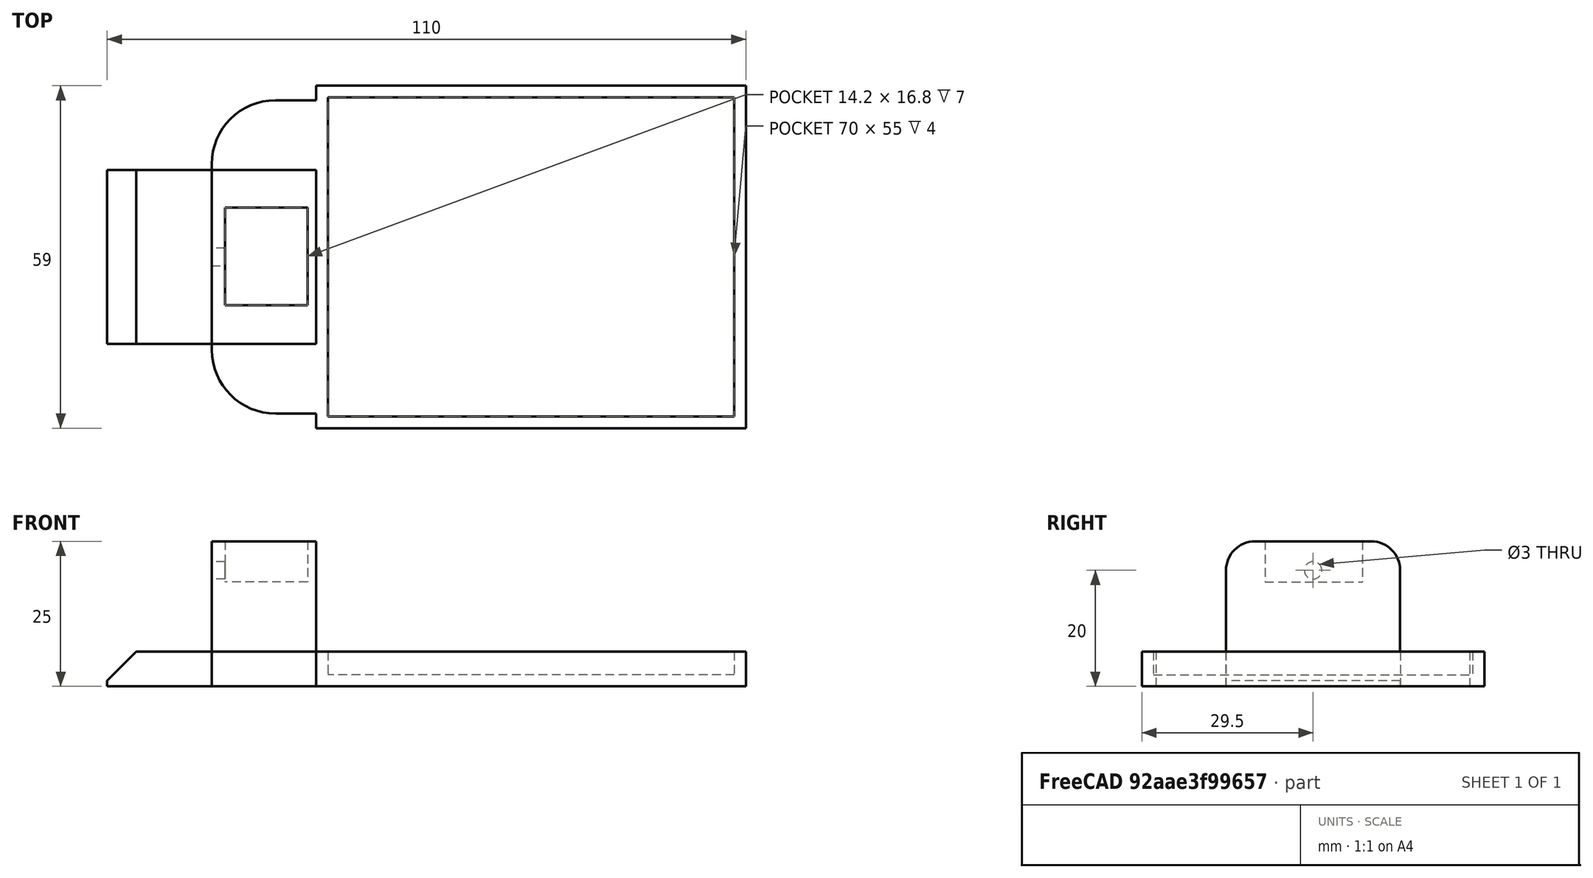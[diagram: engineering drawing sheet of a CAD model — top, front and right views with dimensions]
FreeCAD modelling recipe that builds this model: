
FCSTD DOCUMENT  (FreeCAD 0.18R4 (GitTag))
Label: keyboardSWPart6
License: All rights reserved
LicenseURL: http://en.wikipedia.org/wiki/All_rights_reserved
objects: Mesh::Feature×13, Sketcher::SketchObject×8, PartDesign::Pad×5, PartDesign::Pocket×3, PartDesign::Fillet×3, PartDesign::Chamfer×1, PartDesign::Body×1
note: 29 computed .brp shape members not serialized (recipe doc carries the construction recipe); baked Part::Feature solids carry a one-line shape summary decoded from their .brp

FEATURE [Sketcher::SketchObject] Sketch
  MapMode = 5
  Support = -> [XY_Plane]
  sketch-geometry (4):
    g0: LineSegment StartX=0 StartY=0 StartZ=0 EndX=74 EndY=0 EndZ=0
    g1: LineSegment StartX=74 StartY=0 StartZ=0 EndX=74 EndY=59 EndZ=0
    g2: LineSegment StartX=74 StartY=59 StartZ=0 EndX=0 EndY=59 EndZ=0
    g3: LineSegment StartX=0 StartY=59 StartZ=0 EndX=0 EndY=0 EndZ=0
  constraints (11):
    c: Coincident(g0,g1)
    c: Coincident(g1,g2)
    c: Coincident(g2,g3)
    c: Coincident(g3,g0)
    c: Horizontal(g0)
    c: Horizontal(g2)
    c: Vertical(g1)
    c: Vertical(g3)
    c: DistanceX(g2,g2) = 74
    c: DistanceY(g1,g1) = 59
    c: Coincident(g-1,g0)
FEATURE [PartDesign::Pad] Pad
  Length = 6
  Length2 = 100
  Profile = -> Sketch
  Type = 0
FEATURE [Sketcher::SketchObject] Sketch001
  MapMode = 5
  Placement = pos=(0,0,6) rot=(0,0,1;0rad)
  Support = -> [Pad]
  sketch-geometry (4):
    g0: LineSegment StartX=2 StartY=57 StartZ=0 EndX=72 EndY=57 EndZ=0
    g1: LineSegment StartX=72 StartY=57 StartZ=0 EndX=72 EndY=2 EndZ=0
    g2: LineSegment StartX=72 StartY=2 StartZ=0 EndX=2 EndY=2 EndZ=0
    g3: LineSegment StartX=2 StartY=2 StartZ=0 EndX=2 EndY=57 EndZ=0
  constraints (12):
    c: Coincident(g0,g1)
    c: Coincident(g1,g2)
    c: Coincident(g2,g3)
    c: Coincident(g3,g0)
    c: Horizontal(g0)
    c: Horizontal(g2)
    c: Vertical(g1)
    c: Vertical(g3)
    c: DistanceX(g0,g0) = 70
    c: DistanceY(g3,g3) = 55
    c: DistanceX(g-1,g2) = 2
    c: DistanceY(g-1,g2) = 2
FEATURE [PartDesign::Pocket] Pocket
  BaseFeature = -> Pad
  Length = 4
  Length2 = 100
  Profile = -> Sketch001
  Type = 0
FEATURE [Sketcher::SketchObject] Sketch002
  MapMode = 5
  Placement = pos=(0,0,0) rot=(0.57735,-0.57735,-0.57735;2.0944rad)
  Support = -> [Pocket]
  sketch-geometry (4):
    g0: LineSegment StartX=-14.5 StartY=0 StartZ=0 EndX=-44.5 EndY=0 EndZ=0
    g1: LineSegment StartX=-44.5 StartY=0 StartZ=0 EndX=-44.5 EndY=25 EndZ=0
    g2: LineSegment StartX=-44.5 StartY=25 StartZ=0 EndX=-14.5 EndY=25 EndZ=0
    g3: LineSegment StartX=-14.5 StartY=25 StartZ=0 EndX=-14.5 EndY=0 EndZ=0
  constraints (12):
    c: Coincident(g0,g1)
    c: Coincident(g1,g2)
    c: Coincident(g2,g3)
    c: Coincident(g3,g0)
    c: Horizontal(g0)
    c: Horizontal(g2)
    c: Vertical(g1)
    c: Vertical(g3)
    c: PointOnObject(g0,g-1)
    c: DistanceX(g2,g2) = 30
    c: DistanceX(g0,g-1) = 14.5
    c: DistanceY(g1,g1) = 25
FEATURE [PartDesign::Pad] Pad001
  BaseFeature = -> Pocket
  Length = 18
  Length2 = 100
  Profile = -> Sketch002
  Type = 0
FEATURE [Sketcher::SketchObject] Sketch003
  MapMode = 5
  Placement = pos=(0,0,25) rot=(0,0,1;0rad)
  Support = -> [Pad001]
  sketch-geometry (4):
    g0: LineSegment StartX=-15.7 StartY=38 StartZ=0 EndX=-1.5 EndY=38 EndZ=0
    g1: LineSegment StartX=-1.5 StartY=38 StartZ=0 EndX=-1.5 EndY=21.2 EndZ=0
    g2: LineSegment StartX=-1.5 StartY=21.2 StartZ=0 EndX=-15.7 EndY=21.2 EndZ=0
    g3: LineSegment StartX=-15.7 StartY=21.2 StartZ=0 EndX=-15.7 EndY=38 EndZ=0
  constraints (12):
    c: Coincident(g0,g1)
    c: Coincident(g1,g2)
    c: Coincident(g2,g3)
    c: Coincident(g3,g0)
    c: Horizontal(g0)
    c: Horizontal(g2)
    c: Vertical(g1)
    c: Vertical(g3)
    c: DistanceX(g0,g0) = 14.2
    c: DistanceY(g3,g3) = 16.8
    c: DistanceX(g1,g-1) = 1.5
    c: DistanceY(g-1,g1) = 21.2
FEATURE [PartDesign::Pocket] Pocket001
  BaseFeature = -> Pad001
  Length = 7
  Length2 = 100
  Profile = -> Sketch003
  Type = 0
FEATURE [PartDesign::Fillet] Fillet
  Base = -> Pocket001 [Edge39,Edge21]
  BaseFeature = -> Pocket001
  Radius = 5
FEATURE [Sketcher::SketchObject] Sketch004
  MapMode = 5
  Placement = pos=(-18,0,0) rot=(0.57735,-0.57735,-0.57735;2.0944rad)
  Support = -> [Fillet]
  sketch-geometry (1):
    g0: Circle CenterX=-29.5 CenterY=20 CenterZ=0 NormalX=0 NormalY=0 NormalZ=1 AngleXU=0 Radius=1.5
  constraints (3):
    c: Radius(g0) = 1.5
    c: DistanceX(g0,g-1) = 29.5
    c: DistanceY(g-1,g0) = 20
FEATURE [PartDesign::Pocket] Pocket002
  BaseFeature = -> Fillet
  Length = 5
  Length2 = 100
  Profile = -> Sketch004
  Type = 0
FEATURE [Sketcher::SketchObject] Sketch005
  MapMode = 5
  Placement = pos=(0,44.5,0) rot=(0,0.707107,0.707107;3.14159rad)
  Support = -> [Pocket002]
  sketch-geometry (4):
    g0: LineSegment StartX=0 StartY=6 StartZ=0 EndX=18.0086 EndY=6 EndZ=0
    g1: LineSegment StartX=18.0086 StartY=6 StartZ=0 EndX=18.0086 EndY=0 EndZ=0
    g2: LineSegment StartX=18.0086 StartY=0 StartZ=0 EndX=0 EndY=0 EndZ=0
    g3: LineSegment StartX=0 StartY=0 StartZ=0 EndX=0 EndY=6 EndZ=0
  constraints (10):
    c: Coincident(g0,g1)
    c: Coincident(g1,g2)
    c: Coincident(g2,g3)
    c: Coincident(g3,g0)
    c: Horizontal(g0)
    c: Horizontal(g2)
    c: Vertical(g1)
    c: Vertical(g3)
    c: Coincident(g2,g-1)
    c: DistanceY(g1,g1) = 6
FEATURE [PartDesign::Pad] Pad002
  BaseFeature = -> Pocket002
  Length = 12
  Length2 = 100
  Profile = -> Sketch005
  Type = 0
FEATURE [PartDesign::Fillet] Fillet001
  Base = -> Pad002 [Edge74]
  BaseFeature = -> Pad002
  Radius = 11
FEATURE [Sketcher::SketchObject] Sketch006
  MapMode = 5
  Placement = pos=(0,14.5,0) rot=(1,0,0;1.5708rad)
  Support = -> [Fillet001]
  sketch-geometry (4):
    g0: LineSegment StartX=0 StartY=0 StartZ=0 EndX=-17.9686 EndY=0 EndZ=0
    g1: LineSegment StartX=-17.9686 StartY=0 StartZ=0 EndX=-17.9686 EndY=6 EndZ=0
    g2: LineSegment StartX=-17.9686 StartY=6 StartZ=0 EndX=0 EndY=6 EndZ=0
    g3: LineSegment StartX=0 StartY=6 StartZ=0 EndX=0 EndY=0 EndZ=0
  constraints (10):
    c: Coincident(g0,g1)
    c: Coincident(g1,g2)
    c: Coincident(g2,g3)
    c: Coincident(g3,g0)
    c: Horizontal(g0)
    c: Horizontal(g2)
    c: Vertical(g1)
    c: Vertical(g3)
    c: Coincident(g0,g-1)
    c: DistanceY(g1,g1) = 6
FEATURE [PartDesign::Pad] Pad003
  BaseFeature = -> Fillet001
  Length = 12
  Length2 = 100
  Profile = -> Sketch006
  Type = 0
FEATURE [PartDesign::Fillet] Fillet002
  Base = -> Pad003 [Edge69]
  BaseFeature = -> Pad003
  Radius = 11
FEATURE [Sketcher::SketchObject] Sketch007
  MapMode = 5
  Placement = pos=(-18,0,0) rot=(0.57735,-0.57735,-0.57735;2.0944rad)
  Support = -> [Fillet002]
  sketch-geometry (4):
    g0: LineSegment StartX=-14.5223 StartY=0 StartZ=0 EndX=-44.5193 EndY=0 EndZ=0
    g1: LineSegment StartX=-44.5193 StartY=0 StartZ=0 EndX=-44.5193 EndY=6 EndZ=0
    g2: LineSegment StartX=-44.5193 StartY=6 StartZ=0 EndX=-14.5223 EndY=6 EndZ=0
    g3: LineSegment StartX=-14.5223 StartY=6 StartZ=0 EndX=-14.5223 EndY=0 EndZ=0
  constraints (10):
    c: Coincident(g0,g1)
    c: Coincident(g1,g2)
    c: Coincident(g2,g3)
    c: Coincident(g3,g0)
    c: Horizontal(g0)
    c: Horizontal(g2)
    c: Vertical(g1)
    c: Vertical(g3)
    c: DistanceY(g3,g3) = 6
    c: DistanceY(g-1,g0) = 0
FEATURE [PartDesign::Pad] Pad004
  BaseFeature = -> Fillet002
  Length = 18
  Length2 = 100
  Profile = -> Sketch007
  Type = 0
FEATURE [PartDesign::Chamfer] Chamfer
  Base = -> Pad004 [Edge76]
  BaseFeature = -> Pad004
  Size = 5
FEATURE [PartDesign::Body] Body
  Group = -> [Sketch,Pad,Sketch001,Pocket,Sketch002,Pad001,Sketch003,Pocket001,Fillet,Sketch004,Pocket002,Sketch005,Pad002,Fillet001,Sketch006,Pad003,Fillet002,Sketch007,Pad004,Chamfer]
  Origin = -> Origin
  Tip = -> Chamfer
FEATURE [Mesh::Feature] Mesh  label="Body (Meshed)"
FEATURE [Mesh::Feature] Mesh001  label="Pad (Meshed)"
FEATURE [Mesh::Feature] Mesh002  label="Pocket (Meshed)"
FEATURE [Mesh::Feature] Mesh003  label="Pad001 (Meshed)"
FEATURE [Mesh::Feature] Mesh004  label="Pocket001 (Meshed)"
FEATURE [Mesh::Feature] Mesh005  label="Fillet (Meshed)"
FEATURE [Mesh::Feature] Mesh006  label="Pocket002 (Meshed)"
FEATURE [Mesh::Feature] Mesh007  label="Pad002 (Meshed)"
FEATURE [Mesh::Feature] Mesh008  label="Fillet001 (Meshed)"
FEATURE [Mesh::Feature] Mesh009  label="Pad003 (Meshed)"
FEATURE [Mesh::Feature] Mesh010  label="Fillet002 (Meshed)"
FEATURE [Mesh::Feature] Mesh011  label="Pad004 (Meshed)"
FEATURE [Mesh::Feature] Mesh012  label="Chamfer (Meshed)"
